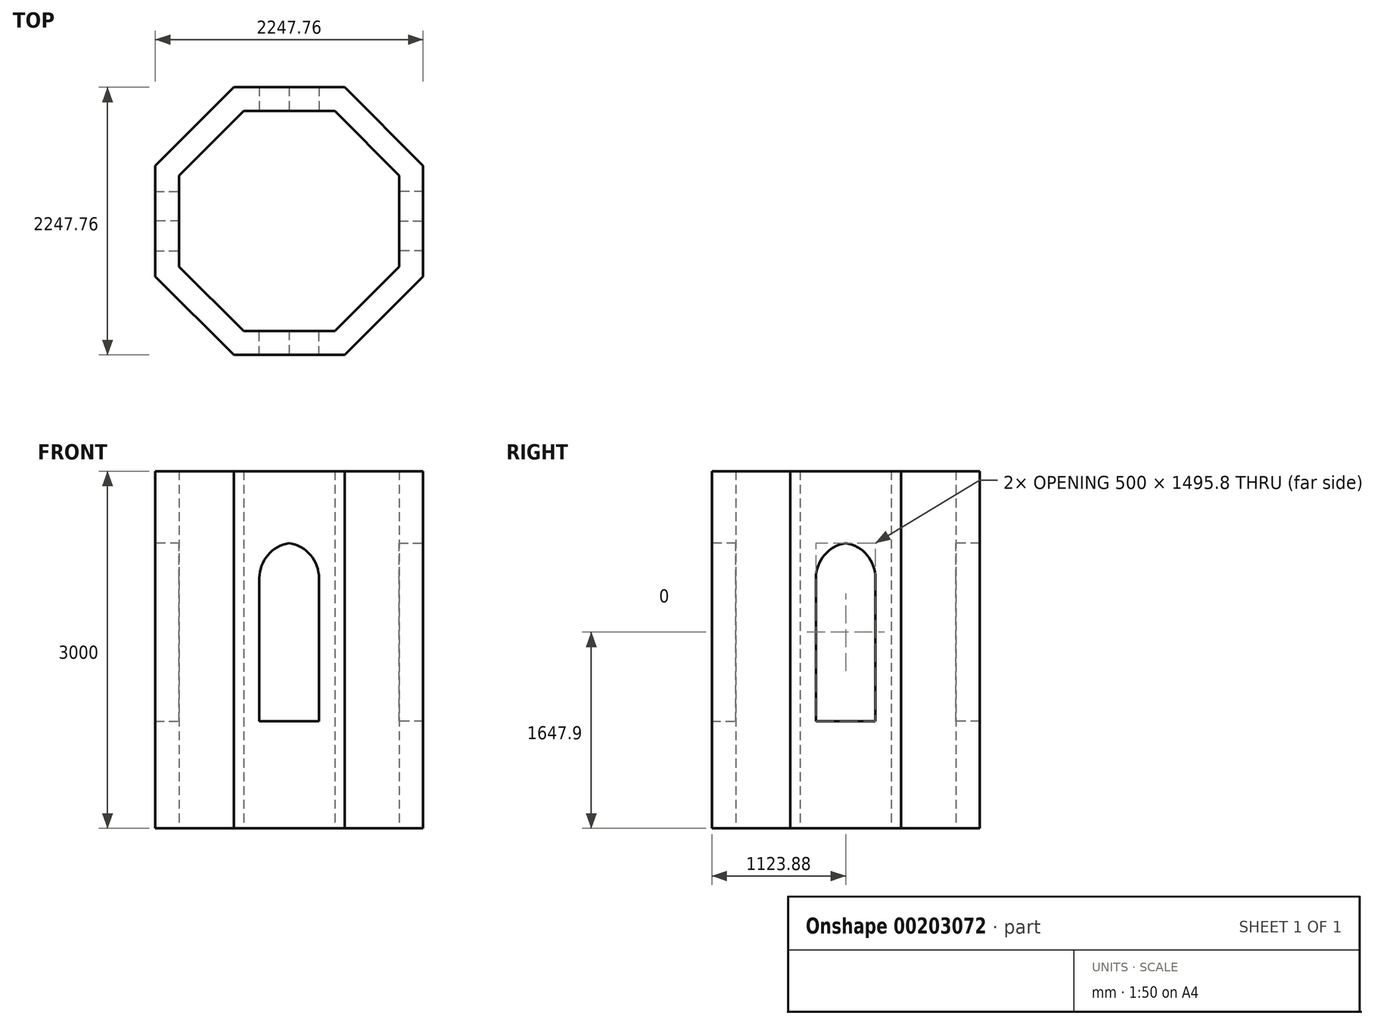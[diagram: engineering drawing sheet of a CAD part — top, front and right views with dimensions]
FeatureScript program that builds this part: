
annotation { "Feature Type Name" : "Feature", "Feature Type Description" : "" }
export const myFeature = defineFeature(function(context is Context, id is Id, definition is map)
    precondition{}
    {
        {
            assignVariable(context, id + "F0", {"name" : "baraban", "anyValue" : 3000});
        }
        {
            var Q0;
            Q0=qCreatedBy(makeId("Top.planeOp"),FACE);
            var sketch = newSketch(context, id + "F1", { "sketchPlane" : qUnion([Q0])});
            skCircle(sketch, "E0.cCircle", {"center": v(0, 0) * mm, "radius": 1000 * mm, "construction": true});
            skLineSegment(sketch, "E0.0", {"start": v(-382.68, 923.88) * mm, "end": v(382.68, 923.88) * mm});
            skLineSegment(sketch, "E0.1", {"start": v(382.68, 923.88) * mm, "end": v(923.88, 382.68) * mm});
            skLineSegment(sketch, "E0.2", {"start": v(923.88, 382.68) * mm, "end": v(923.88, -382.68) * mm});
            skLineSegment(sketch, "E0.3", {"start": v(923.88, -382.68) * mm, "end": v(382.68, -923.88) * mm});
            skLineSegment(sketch, "E0.4", {"start": v(382.68, -923.88) * mm, "end": v(-382.68, -923.88) * mm});
            skLineSegment(sketch, "E0.5", {"start": v(-382.68, -923.88) * mm, "end": v(-923.88, -382.68) * mm});
            skLineSegment(sketch, "E0.6", {"start": v(-923.88, -382.68) * mm, "end": v(-923.88, 382.68) * mm});
            skLineSegment(sketch, "E0.7", {"start": v(-923.88, 382.68) * mm, "end": v(-382.68, 923.88) * mm});
            skLineSegment(sketch, "E1", {"start": v(0, 0) * mm, "end": v(-1362.35, 0) * mm, "construction": true});
            skLineSegment(sketch, "E2.0", {"start": v(465.53, 1123.88) * mm, "end": v(1123.88, 465.53) * mm});
            skLineSegment(sketch, "E2.1", {"start": v(-465.53, 1123.88) * mm, "end": v(465.53, 1123.88) * mm});
            skLineSegment(sketch, "E2.2", {"start": v(1123.88, 465.53) * mm, "end": v(1123.88, -465.53) * mm});
            skLineSegment(sketch, "E2.3", {"start": v(-1123.88, 465.53) * mm, "end": v(-465.53, 1123.88) * mm});
            skLineSegment(sketch, "E2.4", {"start": v(1123.88, -465.53) * mm, "end": v(465.53, -1123.88) * mm});
            skLineSegment(sketch, "E2.5", {"start": v(465.53, -1123.88) * mm, "end": v(-465.53, -1123.88) * mm});
            skLineSegment(sketch, "E2.6", {"start": v(-465.53, -1123.88) * mm, "end": v(-1123.88, -465.53) * mm});
            skLineSegment(sketch, "E2.7", {"start": v(-1123.88, -465.53) * mm, "end": v(-1123.88, 465.53) * mm});
            skSolve(sketch);
        }
        {
            var Q0;
            Q0 = qSketchRegion(id + "F1", true);
            extrude(context, id + "F2", {"entities" : qUnion([Q0]), "depth" : (getVariable(context, 'baraban')) * mm});
        }
        {
            var Q0;
            Q0=makeQuery(id+"F2.opExtrude","CAP_FACE",FACE,{"disambiguationData":[OSD([sQuery(id+"F1.wireOp",EDGE,"E0.0"),sQuery(id+"F1.wireOp",EDGE,"E0.1"),sQuery(id+"F1.wireOp",EDGE,"E0.2"),sQuery(id+"F1.wireOp",EDGE,"E0.3"),sQuery(id+"F1.wireOp",EDGE,"E0.4"),sQuery(id+"F1.wireOp",EDGE,"E0.5"),sQuery(id+"F1.wireOp",EDGE,"E0.6"),sQuery(id+"F1.wireOp",EDGE,"E0.7")])],"isStart":false});
            var sketch = newSketch(context, id + "F3", { "sketchPlane" : qUnion([Q0])});
            skLineSegment(sketch, "E3.bottom", {"start": v(1400, 250) * mm, "end": v(800, 250) * mm});
            skLineSegment(sketch, "E3.top", {"start": v(1400, -250) * mm, "end": v(800, -250) * mm});
            skLineSegment(sketch, "E3.left", {"start": v(1400, 250) * mm, "end": v(1400, -250) * mm});
            skLineSegment(sketch, "E3.right", {"start": v(800, 250) * mm, "end": v(800, -250) * mm});
            skLineSegment(sketch, "E4", {"start": v(0, 0) * mm, "end": v(1856.66, 0) * mm, "construction": true});
            skPoint(sketch, "E5", {"position": v(800, 0) * mm});
            skLineSegment(sketch, "E6.2.0", {"start": v(250, 1400) * mm, "end": v(250, 800) * mm});
            skLineSegment(sketch, "E6.2.1", {"start": v(-250, 1400) * mm, "end": v(250, 1400) * mm});
            skLineSegment(sketch, "E6.2.2", {"start": v(-250, 1400) * mm, "end": v(-250, 800) * mm});
            skLineSegment(sketch, "E6.2.3", {"start": v(-250, 800) * mm, "end": v(250, 800) * mm});
            skLineSegment(sketch, "E6.4.0", {"start": v(-1400, 250) * mm, "end": v(-800, 250) * mm});
            skLineSegment(sketch, "E6.4.1", {"start": v(-1400, -250) * mm, "end": v(-1400, 250) * mm});
            skLineSegment(sketch, "E6.4.2", {"start": v(-1400, -250) * mm, "end": v(-800, -250) * mm});
            skLineSegment(sketch, "E6.4.3", {"start": v(-800, -250) * mm, "end": v(-800, 250) * mm});
            skLineSegment(sketch, "E6.6.0", {"start": v(-250, -1400) * mm, "end": v(-250, -800) * mm});
            skLineSegment(sketch, "E6.6.1", {"start": v(250, -1400) * mm, "end": v(-250, -1400) * mm});
            skLineSegment(sketch, "E6.6.2", {"start": v(250, -1400) * mm, "end": v(250, -800) * mm});
            skLineSegment(sketch, "E6.6.3", {"start": v(250, -800) * mm, "end": v(-250, -800) * mm});
            skPoint(sketch, "E6.center", {"position": v(0, 0) * mm});
            skSolve(sketch);
        }
        {
            var Q0;
            Q0 = qSketchRegion(id + "F3", true);
            extrude(context, id + "F4", {"entities" : qUnion([Q0]), "oppositeDirection" : true, "offsetDistance" : 25 * mm, "depth" : 2100 * mm, "hasSecondDirection" : true, "secondDirectionOppositeDirection" : true, "secondDirectionDepth" : 600 * mm});
        }
        {
            var Q0;
            Q0=makeQuery(id+"F4.opExtrude","CAP_EDGE",EDGE,{"disambiguationData":[OSD([sQuery(id+"F3.wireOp",EDGE,"E6.2.2")])],"isStart":true});
            var Q1;
            Q1=makeQuery(id+"F4.opExtrude","CAP_EDGE",EDGE,{"disambiguationData":[OSD([sQuery(id+"F3.wireOp",EDGE,"E6.2.0")])],"isStart":true});
            var Q2;
            Q2=makeQuery(id+"F4.opExtrude","CAP_EDGE",EDGE,{"disambiguationData":[OSD([sQuery(id+"F3.wireOp",EDGE,"E6.3.0")])],"isStart":true});
            var Q3;
            Q3=makeQuery(id+"F4.opExtrude","CAP_EDGE",EDGE,{"disambiguationData":[OSD([sQuery(id+"F3.wireOp",EDGE,"E6.3.2")])],"isStart":true});
            var Q4;
            Q4=makeQuery(id+"F4.opExtrude","CAP_EDGE",EDGE,{"disambiguationData":[OSD([sQuery(id+"F3.wireOp",EDGE,"E6.4.0")])],"isStart":true});
            var Q5;
            Q5=makeQuery(id+"F4.opExtrude","CAP_EDGE",EDGE,{"disambiguationData":[OSD([sQuery(id+"F3.wireOp",EDGE,"E6.4.2")])],"isStart":true});
            var Q6;
            Q6=makeQuery(id+"F4.opExtrude","CAP_EDGE",EDGE,{"disambiguationData":[OSD([sQuery(id+"F3.wireOp",EDGE,"E6.5.0")])],"isStart":true});
            var Q7;
            Q7=makeQuery(id+"F4.opExtrude","CAP_EDGE",EDGE,{"disambiguationData":[OSD([sQuery(id+"F3.wireOp",EDGE,"E6.5.2")])],"isStart":true});
            var Q8;
            Q8=makeQuery(id+"F4.opExtrude","CAP_EDGE",EDGE,{"disambiguationData":[OSD([sQuery(id+"F3.wireOp",EDGE,"E6.6.0")])],"isStart":true});
            var Q9;
            Q9=makeQuery(id+"F4.opExtrude","CAP_EDGE",EDGE,{"disambiguationData":[OSD([sQuery(id+"F3.wireOp",EDGE,"E6.6.2")])],"isStart":true});
            var Q10;
            Q10=makeQuery(id+"F4.opExtrude","CAP_EDGE",EDGE,{"disambiguationData":[OSD([sQuery(id+"F3.wireOp",EDGE,"E6.7.0")])],"isStart":true});
            var Q11;
            Q11=makeQuery(id+"F4.opExtrude","CAP_EDGE",EDGE,{"disambiguationData":[OSD([sQuery(id+"F3.wireOp",EDGE,"E6.7.2")])],"isStart":true});
            var Q12;
            Q12=makeQuery(id+"F4.opExtrude","CAP_EDGE",EDGE,{"disambiguationData":[OSD([sQuery(id+"F3.wireOp",EDGE,"E3.top")])],"isStart":true});
            var Q13;
            Q13=makeQuery(id+"F4.opExtrude","CAP_EDGE",EDGE,{"disambiguationData":[OSD([sQuery(id+"F3.wireOp",EDGE,"E3.bottom")])],"isStart":true});
            var Q14;
            Q14=makeQuery(id+"F4.opExtrude","CAP_EDGE",EDGE,{"disambiguationData":[OSD([sQuery(id+"F3.wireOp",EDGE,"E6.1.2")])],"isStart":true});
            var Q15;
            Q15=makeQuery(id+"F4.opExtrude","CAP_EDGE",EDGE,{"disambiguationData":[OSD([sQuery(id+"F3.wireOp",EDGE,"E6.1.0")])],"isStart":true});
            fillet(context, id + "F5", {"entities" : qUnion([Q0, Q1, Q2, Q3, Q4, Q5, Q6, Q7, Q8, Q9, Q10, Q11, Q12, Q13, Q14, Q15]), "radius" : 300 * mm, "tangentPropagation" : true, "allowEdgeOverflow" : false});
        }
        {
            var Q0;
            Q0=makeQuery(id+"F4.opExtrude","SWEPT_BODY",BODY,{"disambiguationData":[OSD([sQuery(id+"F3.wireOp",EDGE,"E6.7.0"),sQuery(id+"F3.wireOp",EDGE,"E6.7.1"),sQuery(id+"F3.wireOp",EDGE,"E6.7.2"),sQuery(id+"F3.wireOp",EDGE,"E6.7.3")])]});
            var Q1;
            Q1=makeQuery(id+"F4.opExtrude","SWEPT_BODY",BODY,{"disambiguationData":[OSD([sQuery(id+"F3.wireOp",EDGE,"E6.6.0"),sQuery(id+"F3.wireOp",EDGE,"E6.6.1"),sQuery(id+"F3.wireOp",EDGE,"E6.6.2"),sQuery(id+"F3.wireOp",EDGE,"E6.6.3")])]});
            var Q2;
            Q2=makeQuery(id+"F4.opExtrude","SWEPT_BODY",BODY,{"disambiguationData":[OSD([sQuery(id+"F3.wireOp",EDGE,"E6.5.0"),sQuery(id+"F3.wireOp",EDGE,"E6.5.1"),sQuery(id+"F3.wireOp",EDGE,"E6.5.2"),sQuery(id+"F3.wireOp",EDGE,"E6.5.3")])]});
            var Q3;
            Q3=makeQuery(id+"F4.opExtrude","SWEPT_BODY",BODY,{"disambiguationData":[OSD([sQuery(id+"F3.wireOp",EDGE,"E6.4.0"),sQuery(id+"F3.wireOp",EDGE,"E6.4.1"),sQuery(id+"F3.wireOp",EDGE,"E6.4.2"),sQuery(id+"F3.wireOp",EDGE,"E6.4.3")])]});
            var Q4;
            Q4=makeQuery(id+"F4.opExtrude","SWEPT_BODY",BODY,{"disambiguationData":[OSD([sQuery(id+"F3.wireOp",EDGE,"E6.3.0"),sQuery(id+"F3.wireOp",EDGE,"E6.3.1"),sQuery(id+"F3.wireOp",EDGE,"E6.3.2"),sQuery(id+"F3.wireOp",EDGE,"E6.3.3")])]});
            var Q5;
            Q5=makeQuery(id+"F4.opExtrude","SWEPT_BODY",BODY,{"disambiguationData":[OSD([sQuery(id+"F3.wireOp",EDGE,"E6.2.0"),sQuery(id+"F3.wireOp",EDGE,"E6.2.1"),sQuery(id+"F3.wireOp",EDGE,"E6.2.2"),sQuery(id+"F3.wireOp",EDGE,"E6.2.3")])]});
            var Q6;
            Q6=makeQuery(id+"F4.opExtrude","SWEPT_BODY",BODY,{"disambiguationData":[OSD([sQuery(id+"F3.wireOp",EDGE,"E6.1.0"),sQuery(id+"F3.wireOp",EDGE,"E6.1.1"),sQuery(id+"F3.wireOp",EDGE,"E6.1.2"),sQuery(id+"F3.wireOp",EDGE,"E6.1.3")])]});
            var Q7;
            Q7=makeQuery(id+"F4.opExtrude","SWEPT_BODY",BODY,{"disambiguationData":[OSD([sQuery(id+"F3.wireOp",EDGE,"E3.bottom"),sQuery(id+"F3.wireOp",EDGE,"E3.top"),sQuery(id+"F3.wireOp",EDGE,"E3.left"),sQuery(id+"F3.wireOp",EDGE,"E3.right")])]});
            var Q8;
            Q8=makeQuery(id+"F2.opExtrude","SWEPT_BODY",BODY,{"disambiguationData":[OSD([sQuery(id+"F1.wireOp",EDGE,"E0.0"),sQuery(id+"F1.wireOp",EDGE,"E0.1"),sQuery(id+"F1.wireOp",EDGE,"E0.2"),sQuery(id+"F1.wireOp",EDGE,"E0.3"),sQuery(id+"F1.wireOp",EDGE,"E0.4"),sQuery(id+"F1.wireOp",EDGE,"E0.5"),sQuery(id+"F1.wireOp",EDGE,"E0.6"),sQuery(id+"F1.wireOp",EDGE,"E0.7")])]});
            booleanBodies(context, id + "F6", {"operationType" : BooleanOperationType.SUBTRACTION, "tools" : qUnion([Q0, Q1, Q2, Q3, Q4, Q5, Q6, Q7]), "targets" : qUnion([Q8])});
        }
    });
